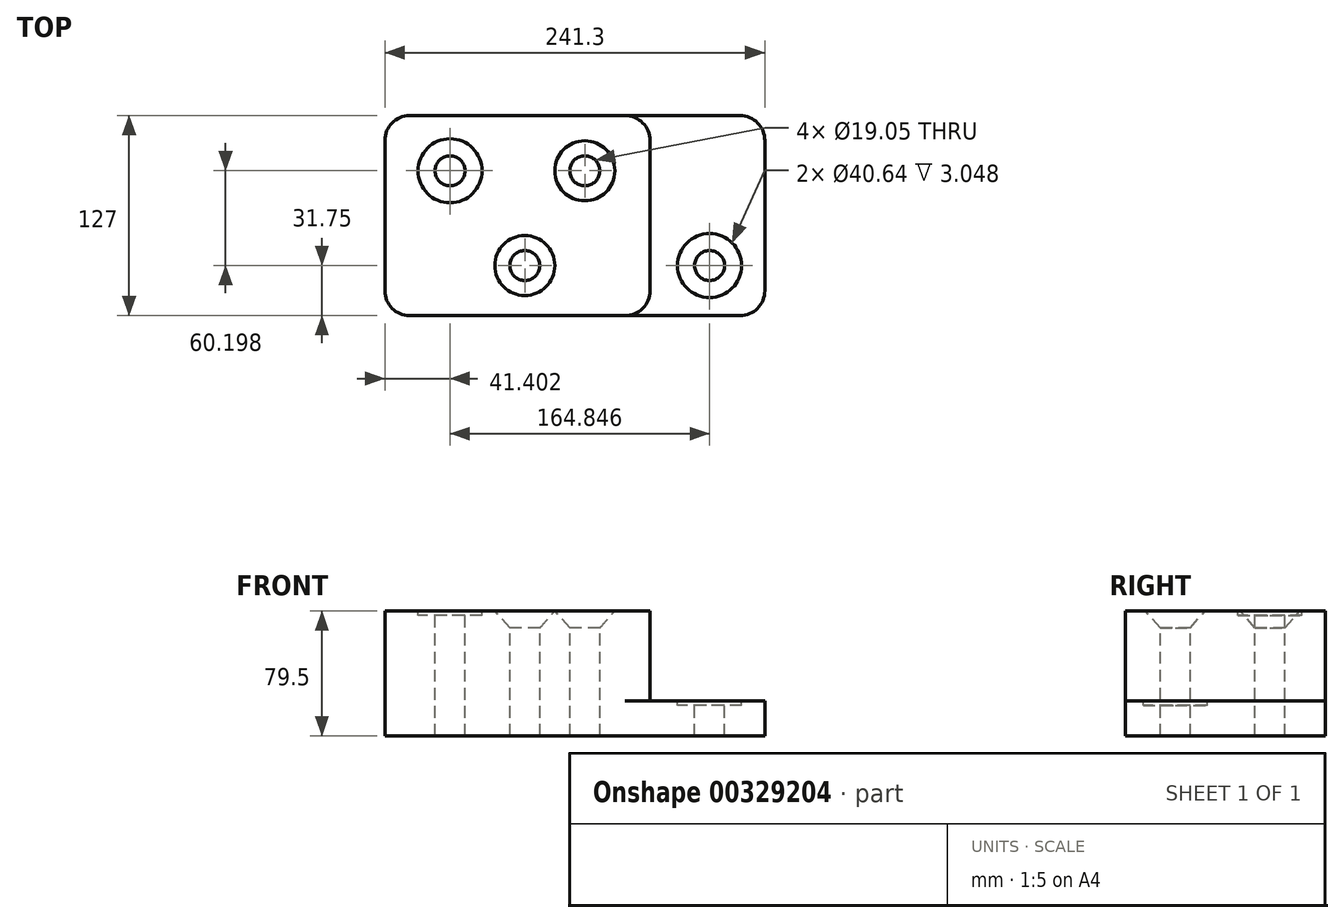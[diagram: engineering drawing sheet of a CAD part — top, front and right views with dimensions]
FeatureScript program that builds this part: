
annotation { "Feature Type Name" : "Feature", "Feature Type Description" : "" }
export const myFeature = defineFeature(function(context is Context, id is Id, definition is map)
    precondition{}
    {
        {
            var Q0;
            Q0=qCreatedBy(makeId("Front.planeOp"),FACE);
            var sketch = newSketch(context, id + "F0", { "sketchPlane" : qUnion([Q0])});
            skLineSegment(sketch, "E0.bottom", {"start": v(0, 0) * mm, "end": v(168.4, 0) * mm});
            skLineSegment(sketch, "E0.top", {"start": v(0, 79.5) * mm, "end": v(168.4, 79.5) * mm});
            skLineSegment(sketch, "E0.left", {"start": v(0, 0) * mm, "end": v(0, 79.5) * mm});
            skLineSegment(sketch, "E0.right", {"start": v(168.4, 0) * mm, "end": v(168.4, 79.5) * mm});
            skLineSegment(sketch, "E1.bottom", {"start": v(168.4, 0) * mm, "end": v(241.3, 0) * mm});
            skLineSegment(sketch, "E1.top", {"start": v(168.4, 22.35) * mm, "end": v(241.3, 22.35) * mm});
            skLineSegment(sketch, "E1.left", {"start": v(168.4, 0) * mm, "end": v(168.4, 22.35) * mm});
            skLineSegment(sketch, "E1.right", {"start": v(241.3, 0) * mm, "end": v(241.3, 22.35) * mm});
            skSolve(sketch);
        }
        {
            var Q0;
            Q0 = qSketchRegion(id + "F0", true);
            extrude(context, id + "F1", {"entities" : qUnion([Q0]), "depth" : 127 * mm});
        }
        {
            var Q0;
            Q0=makeQuery(id+"F1.opExtrude","CAP_EDGE",EDGE,{"disambiguationData":[OSD([sQuery(id+"F0.wireOp",EDGE,"E0.right")])],"isStart":false});
            var Q1;
            Q1=makeQuery(id+"F1.opExtrude","CAP_EDGE",EDGE,{"disambiguationData":[OSD([sQuery(id+"F0.wireOp",EDGE,"E0.right")])],"isStart":true});
            var Q2;
            Q2=makeQuery(id+"F1.opExtrude","CAP_EDGE",EDGE,{"disambiguationData":[OSD([sQuery(id+"F0.wireOp",EDGE,"E1.right")])],"isStart":false});
            var Q3;
            Q3=makeQuery(id+"F1.opExtrude","CAP_EDGE",EDGE,{"disambiguationData":[OSD([sQuery(id+"F0.wireOp",EDGE,"E1.right")])],"isStart":true});
            var Q4;
            Q4=makeQuery(id+"F1.opExtrude","CAP_EDGE",EDGE,{"disambiguationData":[OSD([sQuery(id+"F0.wireOp",EDGE,"E0.left")])],"isStart":false});
            var Q5;
            Q5=makeQuery(id+"F1.opExtrude","CAP_EDGE",EDGE,{"disambiguationData":[OSD([sQuery(id+"F0.wireOp",EDGE,"E0.left")])],"isStart":true});
            fillet(context, id + "F2", {"entities" : qUnion([Q0, Q1, Q2, Q3, Q4, Q5]), "radius" : 15.75 * mm, "tangentPropagation" : true, "allowEdgeOverflow" : false});
        }
        {
            var Q0;
            Q0=makeQuery(id+"F1.opExtrude","SWEPT_FACE",FACE,{"disambiguationData":[OSD([sQuery(id+"F0.wireOp",EDGE,"E0.top")])]});
            var sketch = newSketch(context, id + "F3", { "sketchPlane" : qUnion([Q0])});
            skPoint(sketch, "E2", {"position": v(88.9, -95.25) * mm});
            skPoint(sketch, "E3", {"position": v(41.4, -35.05) * mm});
            skPoint(sketch, "E4", {"position": v(127, -35.05) * mm});
            skPoint(sketch, "E5", {"position": v(206.25, -95.25) * mm});
            skSolve(sketch);
        }
        {
            var Q0;
            Q0=sQuery(id+"F3.wireOp",VERTEX,"E2");
            var Q1;
            Q1=sQuery(id+"F3.wireOp",VERTEX,"E4");
            var Q2;
            Q2=makeQuery(id+"F1.opExtrude","SWEPT_BODY",BODY,{"disambiguationData":[OSD([sQuery(id+"F0.wireOp",EDGE,"E0.bottom"),sQuery(id+"F0.wireOp",EDGE,"E0.top"),sQuery(id+"F0.wireOp",EDGE,"E0.left"),sQuery(id+"F0.wireOp",EDGE,"E0.right"),sQuery(id+"F0.wireOp",EDGE,"E1.bottom"),sQuery(id+"F0.wireOp",EDGE,"E1.top"),sQuery(id+"F0.wireOp",EDGE,"E1.right")])]});
            hole(context, id + "F4", {"style" : HoleStyle.C_SINK, "endStyle" : HoleEndStyle.THROUGH, "holeDiameter" : 19.05 * mm, "cSinkDiameter" : 38.1 * mm, "cSinkAngle" : 82 * degree, "tappedDepth" : 12.7 * mm, "tapClearance" : 3, "locations" : qUnion([Q0, Q1]), "scope" : qUnion([Q2])});
        }
        {
            var Q0;
            Q0=sQuery(id+"F3.wireOp",VERTEX,"E3");
            var Q1;
            Q1=sQuery(id+"F3.wireOp",VERTEX,"E5");
            var Q2;
            Q2=makeQuery(id+"F1.opExtrude","SWEPT_BODY",BODY,{"disambiguationData":[OSD([sQuery(id+"F0.wireOp",EDGE,"E0.bottom"),sQuery(id+"F0.wireOp",EDGE,"E0.top"),sQuery(id+"F0.wireOp",EDGE,"E0.left"),sQuery(id+"F0.wireOp",EDGE,"E0.right"),sQuery(id+"F0.wireOp",EDGE,"E1.bottom"),sQuery(id+"F0.wireOp",EDGE,"E1.top"),sQuery(id+"F0.wireOp",EDGE,"E1.right")])]});
            hole(context, id + "F5", {"style" : HoleStyle.C_BORE, "endStyle" : HoleEndStyle.THROUGH, "holeDiameter" : 19.05 * mm, "cBoreDiameter" : 40.64 * mm, "cBoreDepth" : 3.05 * mm, "tappedDepth" : 12.7 * mm, "tapClearance" : 3, "locations" : qUnion([Q0, Q1]), "scope" : qUnion([Q2])});
        }
    });
